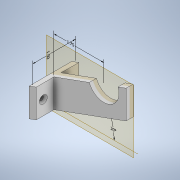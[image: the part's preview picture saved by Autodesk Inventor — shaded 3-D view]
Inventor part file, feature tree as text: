
AUTODESK INVENTOR PART (.ipt)
format: ipt  version: 2021.1 (Build 251245000, 245)  size: 164,864 bytes
history: native  units: in
note: dims shown in document units (in); Inventor stores cm internally (conversion verified against a paired STEP export)
features: sketch x5, other x4, extrude x4, hole x1
ambient origin geometry x8: Origin, YZ Plane, XZ Plane, XY Plane, X Axis, Y Axis, Z Axis, Center Point
bodies: Solid2 (feature_tree)
feature tree (14):
  other  "Annotations"
  extrude  "Extrusion3"  Depth=0.25in
  extrude  "Extrusion4"  Depth=1.5in
  sketch  "Sketch7"  dims[d26=1.075in d29=0.25in]
  extrude  "Extrusion5"  Depth=0.25in
  hole  "Hole3"  [1 undecoded]
  extrude  "Extrusion6"  TaperAngle=0.0deg  [1 undecoded]
  sketch  "Sketch5"  dims[d21=1.0in d22=0.25in]
  sketch  "Sketch6"  dims[d23=1.5in d24=0.0in d25=0.1374in]
  sketch  "Sketch8"  dims[d30=2.0in d31=0.25in]
  sketch  "Sketch9"  dims[d32=0.0in d33=0.0in d34=0.25in d35=0.25in d47=1.5in d48=0.0in d49=0.15in d50=0.75in d51=0.279in d52=0.25in d53=0.5635in d54=1.0in d55=0.8108in d62=1.5in d63=0.0in d56=0.2085in d57=0.331in d58=1.5in d59=2.3174in d60=0.1374in d61=1.75in]
  other  "Linear Dimension 1"
  other  "Angular Dimension 1"
  other  "Linear Dimension 2"
note: 2 required parameter values undecoded (feature->parameter linkage not recoverable at this tier; creation-order binding heuristic only, values carry confidence <= 0.55)
